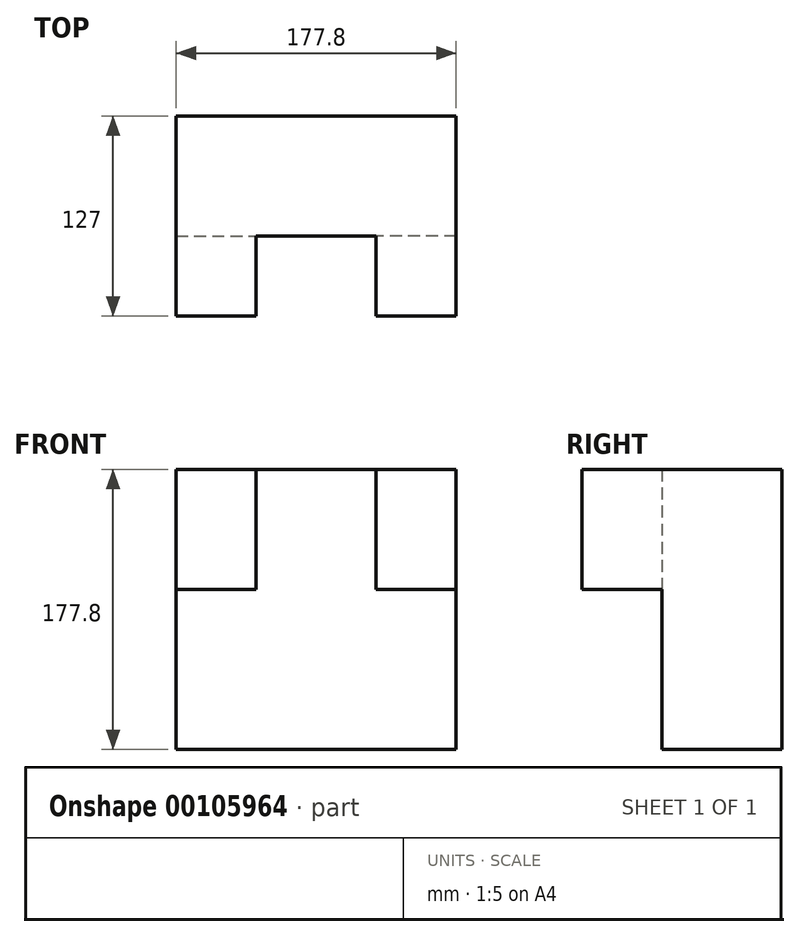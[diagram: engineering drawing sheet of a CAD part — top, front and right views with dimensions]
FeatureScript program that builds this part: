
annotation { "Feature Type Name" : "Feature", "Feature Type Description" : "" }
export const myFeature = defineFeature(function(context is Context, id is Id, definition is map)
    precondition{}
    {
        {
            var Q0;
            Q0=qCreatedBy(makeId("Front.planeOp"),FACE);
            var sketch = newSketch(context, id + "F0", { "sketchPlane" : qUnion([Q0])});
            skLineSegment(sketch, "E0", {"start": v(-87.98, 114.42) * mm, "end": v(-87.98, -63.38) * mm});
            skLineSegment(sketch, "E1", {"start": v(-87.98, -63.38) * mm, "end": v(89.82, -63.38) * mm});
            skLineSegment(sketch, "E2", {"start": v(89.82, -63.38) * mm, "end": v(89.82, 114.42) * mm});
            skLineSegment(sketch, "E3", {"start": v(89.82, 114.42) * mm, "end": v(-87.98, 114.42) * mm});
            skSolve(sketch);
        }
        {
            var Q0;
            Q0 = qSketchRegion(id + "F0", true);
            extrude(context, id + "F1", {"entities" : qUnion([Q0]), "depth" : 50.8 * mm});
        }
        {
            var Q0;
            Q0 = qSketchRegion(id + "FnXB91yH5ofVpva_1", true);
            var Q1;
            Q1=makeQuery(id+"F1.opExtrude","CAP_FACE",FACE,{"disambiguationData":[OSD([sQuery(id+"F0.wireOp",EDGE,"E0"),sQuery(id+"F0.wireOp",EDGE,"E1"),sQuery(id+"F0.wireOp",EDGE,"E2"),sQuery(id+"F0.wireOp",EDGE,"E3")])],"isStart":false});
            extrude(context, id + "F2", {"entities" : qUnion([Q0, Q1]), "operationType" : NewBodyOperationType.ADD, "endBound" : BoundingType.SYMMETRIC, "depth" : 50.8 * mm});
        }
        {
            var Q0;
            Q0=makeQuery(id+"F2.opExtrude","CAP_FACE",FACE,{"disambiguationData":[OSD([sQuery(id+"F0.wireOp",EDGE,"E0"),sQuery(id+"F0.wireOp",EDGE,"E1"),sQuery(id+"F0.wireOp",EDGE,"E2"),sQuery(id+"F0.wireOp",EDGE,"E3")])],"isStart":false});
            var sketch = newSketch(context, id + "F3", { "sketchPlane" : qUnion([Q0])});
            skLineSegment(sketch, "E4.bottom", {"start": v(-87.98, 114.42) * mm, "end": v(-37.18, 114.42) * mm});
            skLineSegment(sketch, "E4.top", {"start": v(-87.98, 38.22) * mm, "end": v(-37.18, 38.22) * mm});
            skLineSegment(sketch, "E4.left", {"start": v(-87.98, 114.42) * mm, "end": v(-87.98, 38.22) * mm});
            skLineSegment(sketch, "E4.right", {"start": v(-37.18, 114.42) * mm, "end": v(-37.18, 38.22) * mm});
            skLineSegment(sketch, "E5.bottom", {"start": v(89.82, 114.42) * mm, "end": v(39.02, 114.42) * mm});
            skLineSegment(sketch, "E5.top", {"start": v(89.82, 38.22) * mm, "end": v(39.02, 38.22) * mm});
            skLineSegment(sketch, "E5.left", {"start": v(89.82, 114.42) * mm, "end": v(89.82, 38.22) * mm});
            skLineSegment(sketch, "E5.right", {"start": v(39.02, 114.42) * mm, "end": v(39.02, 38.22) * mm});
            skSolve(sketch);
        }
        {
            var Q0;
            Q0 = qSketchRegion(id + "F3", true);
            extrude(context, id + "F4", {"entities" : qUnion([Q0]), "operationType" : NewBodyOperationType.ADD, "depth" : 50.8 * mm});
        }
    });
